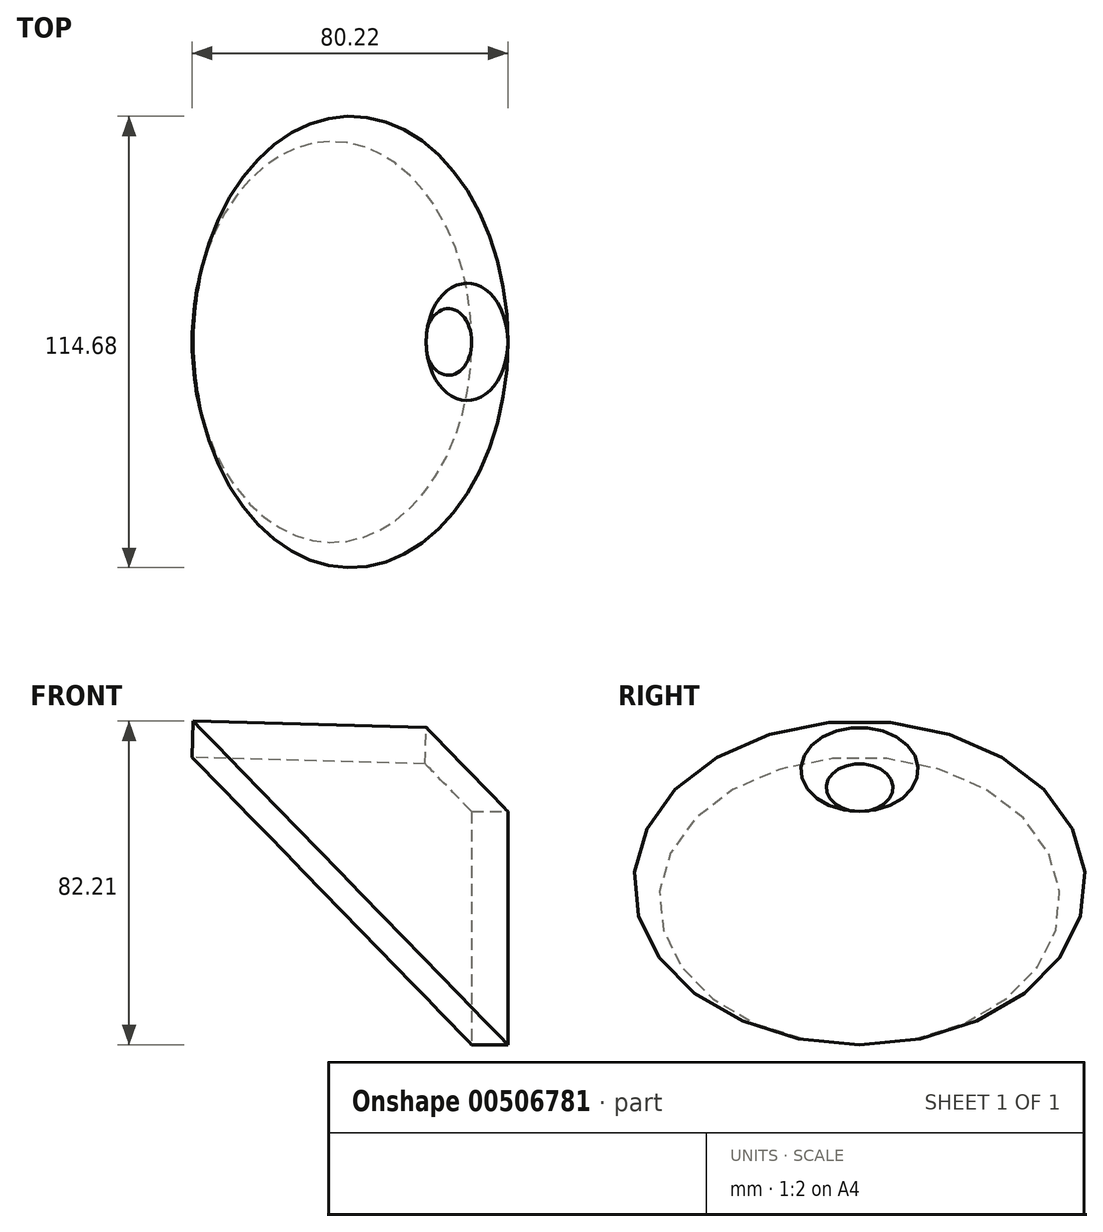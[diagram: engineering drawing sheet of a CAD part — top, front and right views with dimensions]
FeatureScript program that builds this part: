
annotation { "Feature Type Name" : "Feature", "Feature Type Description" : "" }
export const myFeature = defineFeature(function(context is Context, id is Id, definition is map)
    precondition{}
    {
        {
            var Q0;
            Q0=qCreatedBy(makeId("Front.planeOp"),FACE);
            var sketch = newSketch(context, id + "F0", { "sketchPlane" : qUnion([Q0])});
            skLineSegment(sketch, "E0.bottom", {"start": v(30.13, 59.22) * mm, "end": v(39.33, 59.22) * mm});
            skLineSegment(sketch, "E0.top", {"start": v(30.13, 0) * mm, "end": v(39.33, 0) * mm});
            skLineSegment(sketch, "E0.left", {"start": v(30.13, 59.22) * mm, "end": v(30.13, 0) * mm});
            skLineSegment(sketch, "E0.right", {"start": v(39.33, 59.22) * mm, "end": v(39.33, 0) * mm});
            skLineSegment(sketch, "E1", {"start": v(17.37, 58.63) * mm, "end": v(-36.96, 5.79) * mm});
            skSolve(sketch);
        }
        {
            var Q0;
            Q0=makeQuery(id+"F0.imprint","IMPRINT",FACE,{"disambiguationData":[TD([[makeQuery(id+"F0.imprint","IMPRINT",EDGE,{"derivedFrom":sQuery(id+"F0.wireOp",EDGE,"E0.bottom")}),-1.0]])]});
            var Q1;
            Q1=sQuery(id+"F0.wireOp",EDGE,"E1");
            revolve(context, id + "F1", {"entities" : qUnion([Q0]), "axis" : qUnion([Q1]), "revolveType" : RevolveType.FULL});
        }
    });
